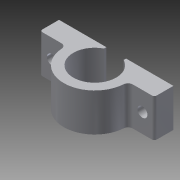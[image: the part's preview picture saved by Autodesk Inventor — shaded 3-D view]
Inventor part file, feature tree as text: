
AUTODESK INVENTOR PART (.ipt)
format: ipt  version: 2014 SP1 (Build 180222100, 222)  size: 154,112 bytes
history: native  units: in
note: dims shown in document units (in); Inventor stores cm internally (conversion verified against a paired STEP export)
features: sketch x2, extrude x2, projected_geometry x2, fillet x1
ambient origin geometry x8: Origin, YZ Plane, XZ Plane, XY Plane, X Axis, Y Axis, Z Axis, Center Point
bodies: Solid1 (feature_tree)
feature tree (7):
  sketch  "Sketch1"  dims[d0=1.5in d1=1.375in d3=1.0in d4=0.0in]
  extrude  "Extrusion1"  Depth=1.0in
  fillet  "Fillet1"  Radius=1.0in
  extrude  "Extrusion3"  Depth=0.75in
  sketch  "Sketch5"  dims[d9=0.5in d10=0.75in d11=0.75in d12=0.5in d14=0.125in d15=0.26in d16=0.26in d17=0.25in d18=0.0in d21=1.125in d22=0.5625in d23=0.0625in d24=1.1875in d25=1.1875in d26=2.375in d34=0.0625in]
  projected_geometry  "Projected Loop1"
  projected_geometry  "Projected Loop2"
